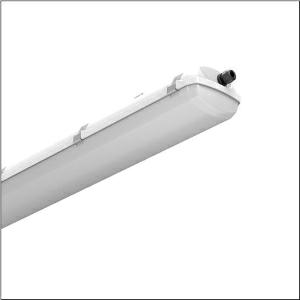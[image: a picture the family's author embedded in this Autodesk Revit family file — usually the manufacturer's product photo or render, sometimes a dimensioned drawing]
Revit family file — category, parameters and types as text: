
# Revit family: monsun_r__ex_51fxa27l460a_7d1b
name_source: partatom
category: Lighting Fixtures
units: mm (PartAtom-declared; Revit-internal decimal feet)

## family parameters
Cut with Voids When Loaded = No
Host = Face
Light Source = No
Part Type = Normal
Room Calculation Point = No
Round Connector Dimension = Use Diameter
Shared = No

## types (1)
- Monsun® Ex (1 x LED, 6560 lm, 53 W, 4000K)
    Apparent Load = 53 VA
    CIE Flux Codes = 46 76 94 98 100
    Color Rendering = 80
    Color Temperature = 4000K
    Default Elevation = 1800 mm
    Description = Monsun® Ex, damp-proof luminaire, primary optical cover: cover, of PC, UV-stabilised, opal, light emission: direct distribution, primary light characteristic: symmetric, installation type: surface-mounted, LED, rated luminous flux: 6.560lm, luminous efficacy: 124lm/W, light colour: 840, colour temperature: 4000K, control gear: ECG, with terminal, 3-pole, max. 2.5mm², through-wiring: 5x 2.5mm², mains connection: 220..250V, AC, 50/60Hz, rated input power: 53W, housing, of PC, light grey (RAL 7035), incl. 1x Ex cable gland M20 for cable diameter 7..12mm with sealing, incl. 1x Ex locking screw M20 with sealing, length: 1.280mm, width: 155mm, height: 105mm, clip for enclosure, of stainless steel, protection rating (complete): IP66, insulation class (complete): insulation class I (protective earthing), certification: CE, explosion class: zone 1,21 II 2G Ex eb mb op is IIC T4 Gb, II 2D Ex tb op is IIIC T67°C Db, impact resistance: IK10, permissible operating ambient temperature: -20..+40°C, contact your sales advisor before using the luminaires in applications with unclear chemical exposure, large temperature fluctuations or condensation-forming humidity, packaging unit: 1 piece
    Height = 105 mm
    Lamp = 1 x LED
    Lamp Light Flux = 6560 lm
    Lamp Power = 53 W
    Lamp count = 1
    Length = 1280 mm
    Luminous efficacy = 124 lm/W
    Manufacturer = Siteco
    ModVariant = No
    Model = 51FXA27L460A
    Mounting Place = Ceiling
    Mounting Type = Surface mounted
    Number of Poles = 1
    OnlyDefault = Yes
    Power Factor = 1
    Product Name = Monsun® Ex
    Product group = damp-proof luminaire
    ProductGroupID = 300
    Protection Class = Protection class I
    Protection Degree = IP 66
    RLX_Detail_Level = 1
    RLX_Emergency_Light_Flux = 0 lm
    RLX_Emergency_Type = 0
    RLX_Emergency_Type_DB = No
    RlxData = <blob elided: 41553 chars, md5=82b23401>
    Socket = socket
    Standby Power = 0 W
    System Light Flux = 6560 lm
    System Power = 53 W
    Type Comments = Product without accessories
    Type Image = l_1258882.jpg
    URL = http://relux.com
    VarID = ---
    Voltage = 0 V
    Weight = 0.00 kg
    Width = 155 mm

## geometry (parser evidence)
native form markers: Blend x4, Sweep x9
no freeform markers — native parametric forms only
